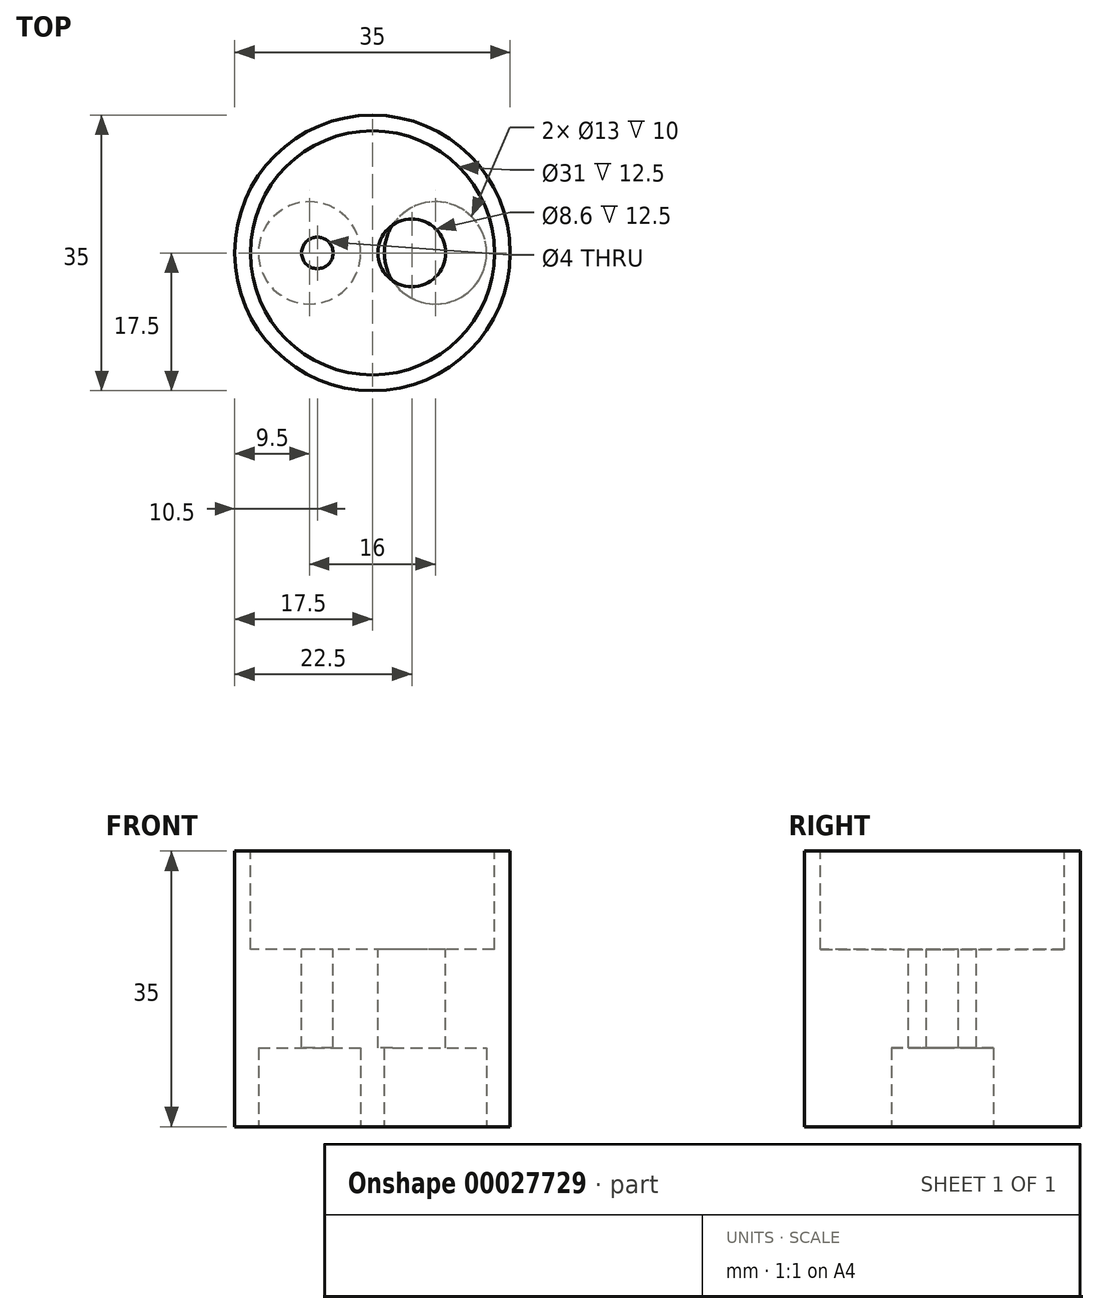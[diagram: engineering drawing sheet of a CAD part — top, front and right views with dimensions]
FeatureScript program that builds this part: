
annotation { "Feature Type Name" : "Feature", "Feature Type Description" : "" }
export const myFeature = defineFeature(function(context is Context, id is Id, definition is map)
    precondition{}
    {
        {
            var Q0;
            Q0=qCreatedBy(makeId("Top.planeOp"),FACE);
            var sketch = newSketch(context, id + "F0", { "sketchPlane" : qUnion([Q0])});
            skCircle(sketch, "E0", {"center": v(0, 0) * mm, "radius": 17.5 * mm});
            skSolve(sketch);
        }
        {
            var Q0;
            Q0=makeQuery(id+"F0.imprint","IMPRINT",FACE,{"disambiguationData":[TD([[makeQuery(id+"F0.imprint","IMPRINT",EDGE,{"derivedFrom":sQuery(id+"F0.wireOp",EDGE,"E0")}),1.0]])]});
            extrude(context, id + "F1", {"entities" : qUnion([Q0]), "depth" : 35 * mm});
        }
        {
            var Q0;
            Q0=makeQuery(id+"F1.opExtrude","CAP_FACE",FACE,{"disambiguationData":[OSD([sQuery(id+"F0.wireOp",EDGE,"E0")])],"isStart":false});
            var sketch = newSketch(context, id + "F2", { "sketchPlane" : qUnion([Q0])});
            skCircle(sketch, "E1", {"center": v(0, 0) * mm, "radius": 15.5 * mm});
            skSolve(sketch);
        }
        {
            var Q0;
            Q0 = qSketchRegion(id + "F2", true);
            var Q1;
            Q1=makeQuery(id+"F2.imprint","IMPRINT",FACE,{"disambiguationData":[TD([[makeQuery(id+"F2.imprint","IMPRINT",EDGE,{"derivedFrom":sQuery(id+"F2.wireOp",EDGE,"E1")}),1.0]])]});
            extrude(context, id + "F3", {"entities" : qUnion([Q0, Q1]), "operationType" : NewBodyOperationType.REMOVE, "oppositeDirection" : true, "depth" : 12.5 * mm});
        }
        {
            var Q0;
            Q0=makeQuery(id+"F3.boolean.opBoolean","COPY",FACE,{"derivedFrom":makeQuery(id+"F3.opExtrude","CAP_FACE",FACE,{"disambiguationData":[OSD([sQuery(id+"F2.wireOp",EDGE,"E1")])],"isStart":false})});
            var sketch = newSketch(context, id + "F4", { "sketchPlane" : qUnion([Q0])});
            skCircle(sketch, "E2", {"center": v(0, 0) * mm, "radius": 10 * mm});
            skCircle(sketch, "E3", {"center": v(5, 0) * mm, "radius": 4.3 * mm});
            skCircle(sketch, "E4", {"center": v(-7, 0) * mm, "radius": 2 * mm});
            skSolve(sketch);
        }
        {
            var Q0;
            Q0=makeQuery(id+"F4.imprint","IMPRINT",FACE,{"disambiguationData":[TD([[makeQuery(id+"F4.imprint","IMPRINT",EDGE,{"derivedFrom":sQuery(id+"F4.wireOp",EDGE,"E4")}),1.0]])]});
            var Q1;
            Q1=makeQuery(id+"F4.imprint","IMPRINT",FACE,{"disambiguationData":[TD([[makeQuery(id+"F4.imprint","IMPRINT",EDGE,{"derivedFrom":sQuery(id+"F4.wireOp",EDGE,"E3")}),1.0]])]});
            extrude(context, id + "F5", {"entities" : qUnion([Q0, Q1]), "operationType" : NewBodyOperationType.REMOVE, "oppositeDirection" : true, "depth" : 12.5 * mm});
        }
        {
            var Q0;
            Q0=makeQuery(id+"F1.opExtrude","CAP_FACE",FACE,{"disambiguationData":[OSD([sQuery(id+"F0.wireOp",EDGE,"E0")])],"isStart":true});
            var sketch = newSketch(context, id + "F6", { "sketchPlane" : qUnion([Q0])});
            skCircle(sketch, "E5", {"center": v(0, 0) * mm, "radius": 16 * mm});
            skCircle(sketch, "E6", {"center": v(-8, 0) * mm, "radius": 6.5 * mm});
            skCircle(sketch, "E7", {"center": v(8, 0) * mm, "radius": 6.5 * mm});
            skSolve(sketch);
        }
        {
            var Q0;
            Q0=makeQuery(id+"F6.imprint","IMPRINT",FACE,{"disambiguationData":[TD([[makeQuery(id+"F6.imprint","IMPRINT",EDGE,{"derivedFrom":sQuery(id+"F6.wireOp",EDGE,"E6")}),1.0]])]});
            var Q1;
            Q1=makeQuery(id+"F6.imprint","IMPRINT",FACE,{"disambiguationData":[TD([[makeQuery(id+"F6.imprint","IMPRINT",EDGE,{"derivedFrom":sQuery(id+"F6.wireOp",EDGE,"E7")}),1.0]])]});
            extrude(context, id + "F7", {"entities" : qUnion([Q0, Q1]), "operationType" : NewBodyOperationType.REMOVE, "oppositeDirection" : true, "depth" : 10 * mm});
        }
    });
